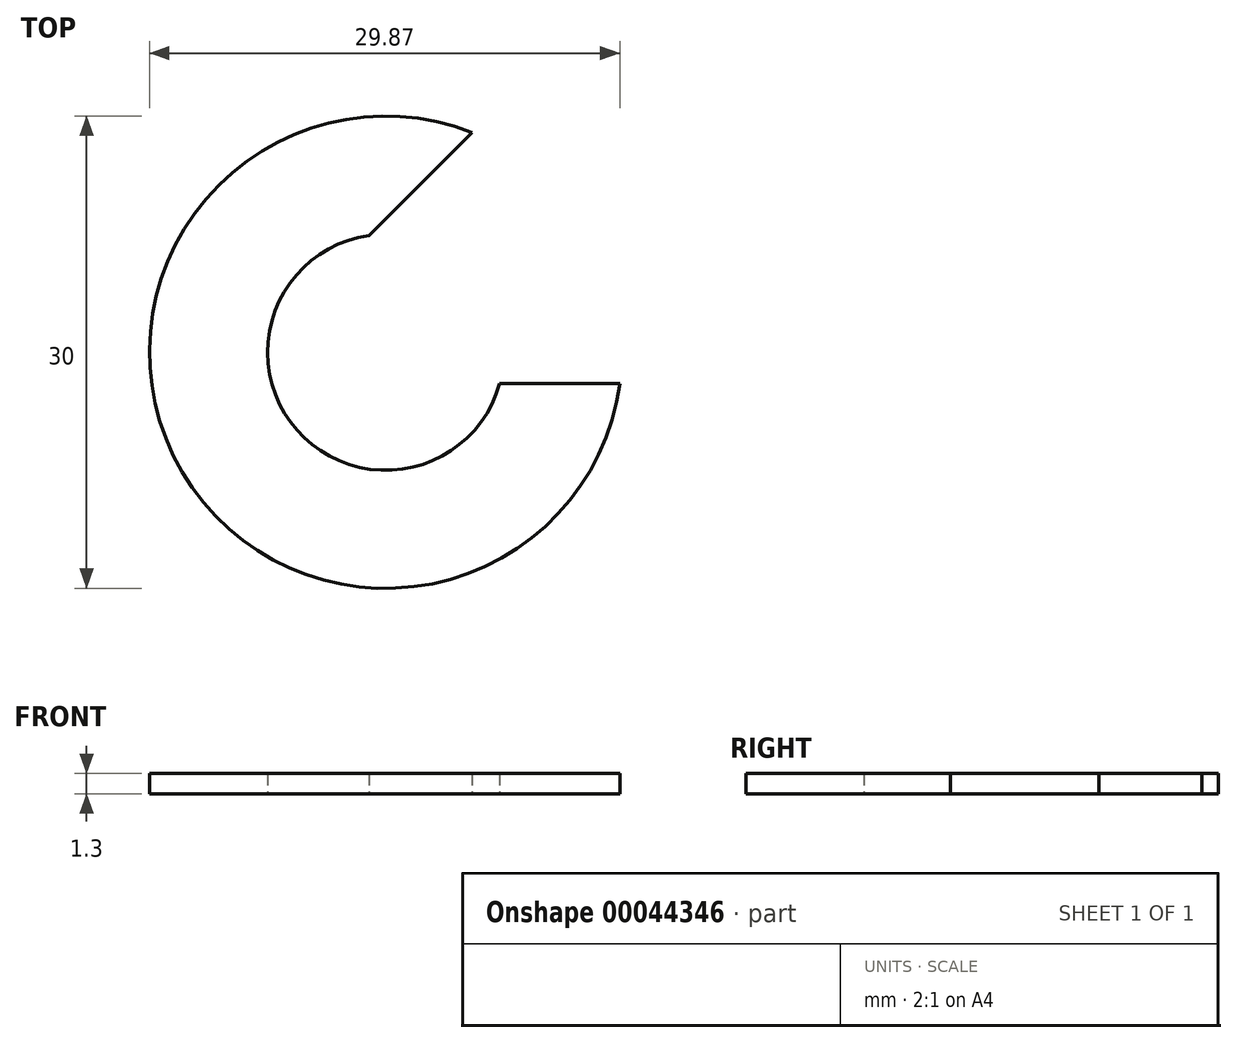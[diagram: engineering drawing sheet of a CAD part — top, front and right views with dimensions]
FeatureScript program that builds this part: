
annotation { "Feature Type Name" : "Feature", "Feature Type Description" : "" }
export const myFeature = defineFeature(function(context is Context, id is Id, definition is map)
    precondition{}
    {
        {
            var Q0;
            Q0=qCreatedBy(makeId("Top.planeOp"),FACE);
            var sketch = newSketch(context, id + "F0", { "sketchPlane" : qUnion([Q0])});
            skArc(sketch, "E0", {"start": v(5.48, 13.96) * mm, "mid": v(-12.93, -7.6) * mm, "end": v(14.87, -2) * mm});
            skArc(sketch, "E1", {"start": v(5.3, 5.3) * mm, "mid": v(-6.93, -2.87) * mm, "end": v(7.5, 0) * mm});
            skLineSegment(sketch, "E2", {"start": v(7.5, 0) * mm, "end": v(15, 0) * mm});
            skLineSegment(sketch, "E3", {"start": v(5.3, 5.3) * mm, "end": v(10.6, 10.6) * mm});
            skLineSegment(sketch, "E4.0", {"start": v(-1.06, 7.42) * mm, "end": v(5.48, 13.96) * mm});
            skLineSegment(sketch, "E5.0", {"start": v(7.23, -2) * mm, "end": v(14.87, -2) * mm});
            skSolve(sketch);
        }
        {
            var Q0;
            Q0 = qSketchRegion(id + "F0", true);
            extrude(context, id + "F1", {"entities" : qUnion([Q0]), "depth" : 1.3 * mm});
        }
    });
